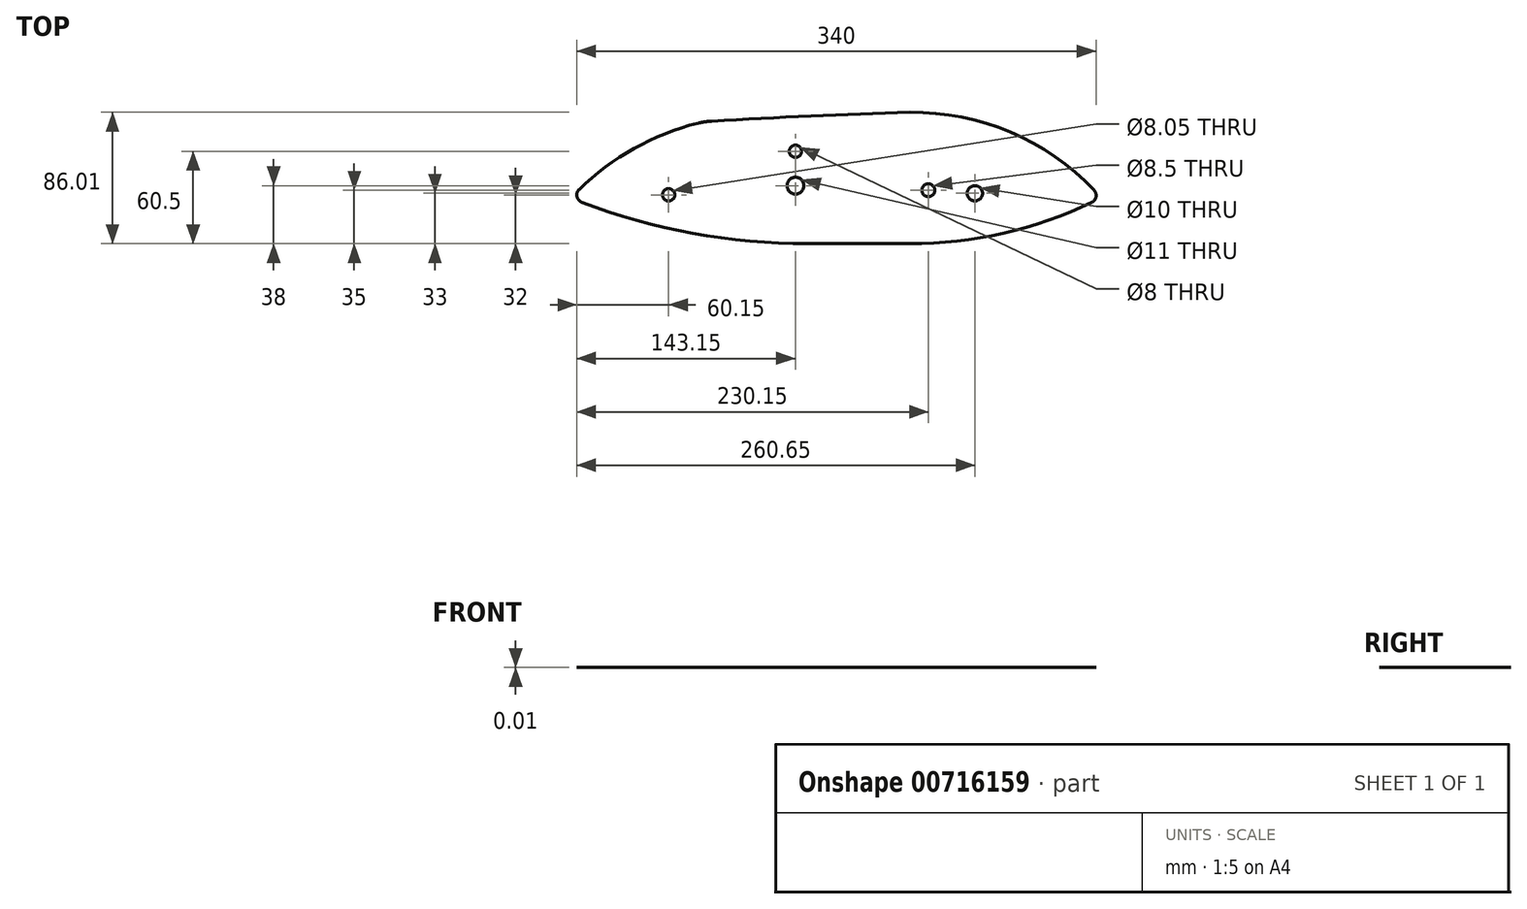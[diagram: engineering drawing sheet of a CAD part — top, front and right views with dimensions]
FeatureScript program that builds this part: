
annotation { "Feature Type Name" : "Feature", "Feature Type Description" : "" }
export const myFeature = defineFeature(function(context is Context, id is Id, definition is map)
    precondition{}
    {
        {
            var Q0;
            Q0=qCreatedBy(makeId("Top.planeOp"),FACE);
            var sketch = newSketch(context, id + "F0", { "sketchPlane" : qUnion([Q0])});
            skLineSegment(sketch, "E0", {"start": v(0, 0) * mm, "end": v(347, 0) * mm, "construction": true});
            skLineSegment(sketch, "E1", {"start": v(155, -30) * mm, "end": v(222, -30) * mm});
            skArc(sketch, "E2", {"start": v(222, 56) * mm, "mid": v(157.1, 53.6) * mm, "end": v(92.22, 50.25) * mm});
            skLineSegment(sketch, "E3", {"start": v(88, 50) * mm, "end": v(88, 0) * mm, "construction": true});
            skLineSegment(sketch, "E4", {"start": v(222, 56) * mm, "end": v(222, 0) * mm, "construction": true});
            skArc(sketch, "E5", {"start": v(83.12, 48.87) * mm, "mid": v(41.34, 32.37) * mm, "end": v(5.35, 5.48) * mm});
            skArc(sketch, "E6", {"start": v(342.48, 4.98) * mm, "mid": v(287.58, 43.11) * mm, "end": v(222, 56) * mm});
            skArc(sketch, "E7", {"start": v(7.07, -2.77) * mm, "mid": v(79.8, -23.14) * mm, "end": v(155, -30) * mm});
            skArc(sketch, "E8", {"start": v(222, -30) * mm, "mid": v(283.02, -23.16) * mm, "end": v(341, -2.96) * mm});
            skLineSegment(sketch, "E9", {"start": v(222, -30) * mm, "end": v(222, 0) * mm, "construction": true});
            skCircle(sketch, "E10", {"center": v(64, 2) * mm, "radius": 4.03 * mm});
            skCircle(sketch, "E11", {"center": v(234, 5) * mm, "radius": 4.25 * mm});
            skCircle(sketch, "E12", {"center": v(264.5, 3) * mm, "radius": 5 * mm});
            skPoint(sketch, "E13.visualSharp", {"position": v(0, 0) * mm});
            skArc(sketch, "E13.filletArc", {"start": v(5.35, 5.48) * mm, "mid": v(3.95, 0.89) * mm, "end": v(7.07, -2.77) * mm});
            skPoint(sketch, "E14.visualSharp", {"position": v(347, 0) * mm});
            skArc(sketch, "E14.filletArc", {"start": v(341, -2.96) * mm, "mid": v(343.76, 0.64) * mm, "end": v(342.48, 4.98) * mm});
            skCircle(sketch, "E15", {"center": v(147, 8) * mm, "radius": 5.5 * mm});
            skCircle(sketch, "E16", {"center": v(147, 30.5) * mm, "radius": 4 * mm});
            skPoint(sketch, "E17.visualSharp", {"position": v(88, 50) * mm});
            skArc(sketch, "E17.filletArc", {"start": v(92.22, 50.25) * mm, "mid": v(87.64, 49.77) * mm, "end": v(83.12, 48.87) * mm});
            skSolve(sketch);
        }
        {
            var Q0;
            Q0 = qSketchRegion(id + "F0", true);
            extrude(context, id + "F1", {"entities" : qUnion([Q0]), "depth" : 1 / 101.6 * mm, "offsetDistance" : 25 * mm});
        }
    });
